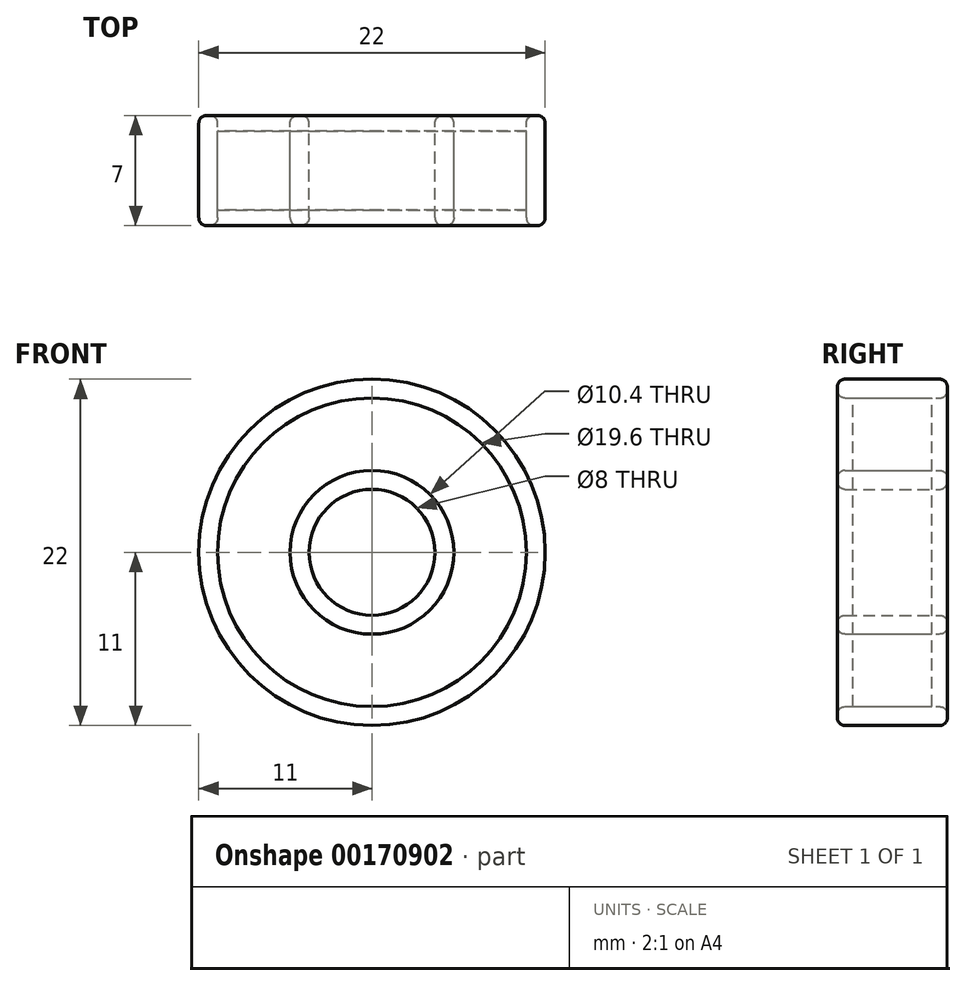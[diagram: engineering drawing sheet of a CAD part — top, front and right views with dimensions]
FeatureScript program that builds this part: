
annotation { "Feature Type Name" : "Feature", "Feature Type Description" : "" }
export const myFeature = defineFeature(function(context is Context, id is Id, definition is map)
    precondition{}
    {
        {
            var Q0;
            Q0=qCreatedBy(makeId("Front.planeOp"),FACE);
            var sketch = newSketch(context, id + "F0", { "sketchPlane" : qUnion([Q0])});
            skCircle(sketch, "E0", {"center": v(0, 0) * mm, "radius": 11 * mm});
            skCircle(sketch, "E1", {"center": v(0, 0) * mm, "radius": 4 * mm});
            skCircle(sketch, "E2.0", {"center": v(0, 0) * mm, "radius": 9.8 * mm});
            skCircle(sketch, "E3.0", {"center": v(0, 0) * mm, "radius": 5.2 * mm});
            skSolve(sketch);
        }
        {
            var Q0;
            Q0=makeQuery(id+"F0.imprint","IMPRINT",FACE,{"disambiguationData":[TD([[makeQuery(id+"F0.imprint","IMPRINT",EDGE,{"derivedFrom":sQuery(id+"F0.wireOp",EDGE,"E0")}),1.0]])]});
            var Q1;
            Q1=makeQuery(id+"F0.imprint","IMPRINT",FACE,{"disambiguationData":[TD([[makeQuery(id+"F0.imprint","IMPRINT",EDGE,{"derivedFrom":sQuery(id+"F0.wireOp",EDGE,"E1")}),-1.0]])]});
            extrude(context, id + "F1", {"entities" : qUnion([Q0, Q1]), "endBound" : BoundingType.SYMMETRIC, "depth" : 7 * mm});
        }
        {
            var Q0;
            Q0=makeQuery(id+"F1.opExtrude","CAP_EDGE",EDGE,{"disambiguationData":[OSD([sQuery(id+"F0.wireOp",EDGE,"E0")])],"isStart":false});
            var Q1;
            Q1=makeQuery(id+"F1.opExtrude","CAP_EDGE",EDGE,{"disambiguationData":[OSD([sQuery(id+"F0.wireOp",EDGE,"E0")])],"isStart":true});
            var Q2;
            Q2=makeQuery(id+"F1.opExtrude","CAP_EDGE",EDGE,{"disambiguationData":[OSD([sQuery(id+"F0.wireOp",EDGE,"E2.0")])],"isStart":false});
            var Q3;
            Q3=makeQuery(id+"F1.opExtrude","CAP_EDGE",EDGE,{"disambiguationData":[OSD([sQuery(id+"F0.wireOp",EDGE,"E2.0")])],"isStart":true});
            var Q4;
            Q4=makeQuery(id+"F1.opExtrude","CAP_EDGE",EDGE,{"disambiguationData":[OSD([sQuery(id+"F0.wireOp",EDGE,"E3.0")])],"isStart":false});
            var Q5;
            Q5=makeQuery(id+"F1.opExtrude","CAP_EDGE",EDGE,{"disambiguationData":[OSD([sQuery(id+"F0.wireOp",EDGE,"E3.0")])],"isStart":true});
            var Q6;
            Q6=makeQuery(id+"F1.opExtrude","CAP_EDGE",EDGE,{"disambiguationData":[OSD([sQuery(id+"F0.wireOp",EDGE,"E1")])],"isStart":false});
            var Q7;
            Q7=makeQuery(id+"F1.opExtrude","CAP_EDGE",EDGE,{"disambiguationData":[OSD([sQuery(id+"F0.wireOp",EDGE,"E1")])],"isStart":true});
            fillet(context, id + "F2", {"entities" : qUnion([Q0, Q1, Q2, Q3, Q4, Q5, Q6, Q7]), "radius" : 0.5 * mm, "tangentPropagation" : true, "allowEdgeOverflow" : false});
        }
        {
            var Q0;
            Q0=makeQuery(id+"F0.imprint","IMPRINT",FACE,{"disambiguationData":[TD([[makeQuery(id+"F0.imprint","IMPRINT",EDGE,{"derivedFrom":sQuery(id+"F0.wireOp",EDGE,"E2.0")}),1.0]])]});
            extrude(context, id + "F3", {"entities" : qUnion([Q0]), "endBound" : BoundingType.SYMMETRIC, "depth" : 5 * mm});
        }
    });
